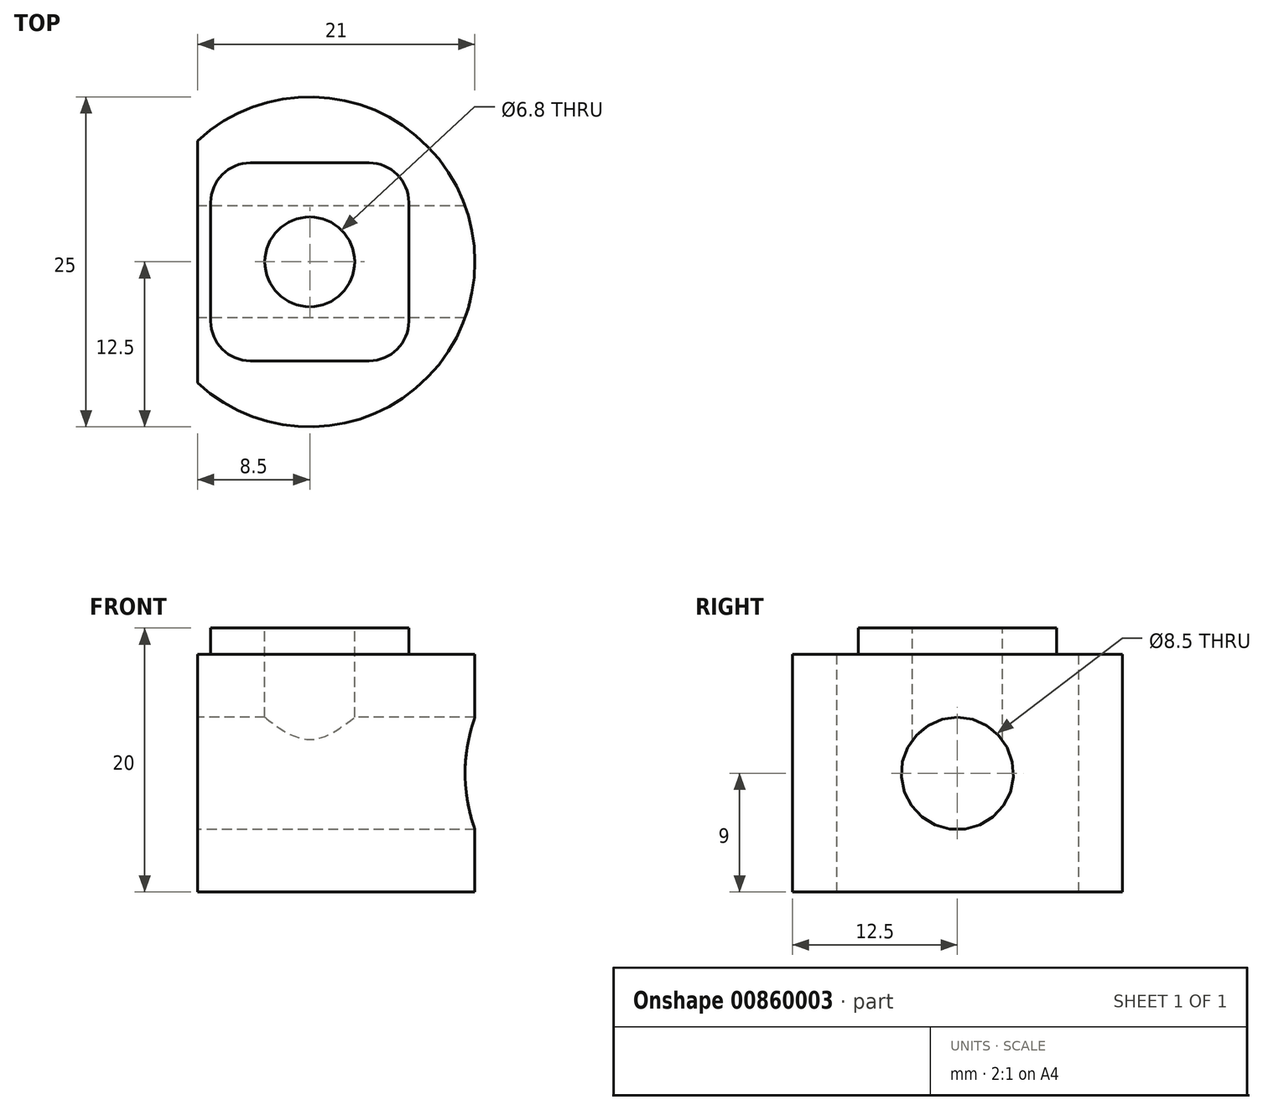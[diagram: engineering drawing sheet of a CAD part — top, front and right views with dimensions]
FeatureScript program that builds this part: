
annotation { "Feature Type Name" : "Feature", "Feature Type Description" : "" }
export const myFeature = defineFeature(function(context is Context, id is Id, definition is map)
    precondition{}
    {
        {
            var Q0;
            Q0=qCreatedBy(makeId("Top.planeOp"),FACE);
            var sketch = newSketch(context, id + "F0", { "sketchPlane" : qUnion([Q0])});
            skArc(sketch, "E0", {"start": v(-8.5, -9.17) * mm, "mid": v(12.5, 0) * mm, "end": v(-8.5, 9.17) * mm});
            skLineSegment(sketch, "E1", {"start": v(-8.5, 9.17) * mm, "end": v(-8.5, -9.17) * mm});
            skSolve(sketch);
        }
        {
            var Q0;
            Q0 = qSketchRegion(id + "F0", true);
            extrude(context, id + "F1", {"entities" : qUnion([Q0]), "depth" : 18 * mm, "offsetDistance" : 25 * mm});
        }
        {
            var Q0;
            Q0=makeQuery(id+"F1.opExtrude","CAP_FACE",FACE,{"disambiguationData":[OSD([sQuery(id+"F0.wireOp",EDGE,"E0"),sQuery(id+"F0.wireOp",EDGE,"E1")])],"isStart":false});
            var sketch = newSketch(context, id + "F2", { "sketchPlane" : qUnion([Q0])});
            skLineSegment(sketch, "E2.bottom", {"start": v(4.5, -7.5) * mm, "end": v(-4.5, -7.5) * mm});
            skLineSegment(sketch, "E2.top", {"start": v(4.5, 7.5) * mm, "end": v(-4.5, 7.5) * mm});
            skLineSegment(sketch, "E2.left", {"start": v(7.5, -4.5) * mm, "end": v(7.5, 4.5) * mm});
            skLineSegment(sketch, "E2.right", {"start": v(-7.5, -4.5) * mm, "end": v(-7.5, 4.5) * mm});
            skPoint(sketch, "E2.middle", {"position": v(0, 0) * mm});
            skPoint(sketch, "E3.visualSharp", {"position": v(-7.5, 7.5) * mm});
            skArc(sketch, "E3.filletArc", {"start": v(-4.5, 7.5) * mm, "mid": v(-6.62, 6.62) * mm, "end": v(-7.5, 4.5) * mm});
            skPoint(sketch, "E4.visualSharp", {"position": v(7.5, 7.5) * mm});
            skArc(sketch, "E4.filletArc", {"start": v(7.5, 4.5) * mm, "mid": v(6.62, 6.62) * mm, "end": v(4.5, 7.5) * mm});
            skPoint(sketch, "E5.visualSharp", {"position": v(7.5, -7.5) * mm});
            skArc(sketch, "E5.filletArc", {"start": v(4.5, -7.5) * mm, "mid": v(6.62, -6.62) * mm, "end": v(7.5, -4.5) * mm});
            skPoint(sketch, "E6.visualSharp", {"position": v(-7.5, -7.5) * mm});
            skArc(sketch, "E6.filletArc", {"start": v(-7.5, -4.5) * mm, "mid": v(-6.62, -6.62) * mm, "end": v(-4.5, -7.5) * mm});
            skSolve(sketch);
        }
        {
            var Q0;
            Q0 = qSketchRegion(id + "F2", true);
            extrude(context, id + "F3", {"entities" : qUnion([Q0]), "operationType" : NewBodyOperationType.ADD, "depth" : 2 * mm, "offsetDistance" : 25 * mm});
        }
        {
            var Q0;
            Q0=makeQuery(id+"F3.opExtrude","CAP_FACE",FACE,{"disambiguationData":[OSD([sQuery(id+"F2.wireOp",EDGE,"E2.bottom"),sQuery(id+"F2.wireOp",EDGE,"E2.top"),sQuery(id+"F2.wireOp",EDGE,"E2.left"),sQuery(id+"F2.wireOp",EDGE,"E2.right"),sQuery(id+"F2.wireOp",EDGE,"E3.filletArc"),sQuery(id+"F2.wireOp",EDGE,"E4.filletArc"),sQuery(id+"F2.wireOp",EDGE,"E5.filletArc"),sQuery(id+"F2.wireOp",EDGE,"E6.filletArc")])],"isStart":false});
            var sketch = newSketch(context, id + "F4", { "sketchPlane" : qUnion([Q0])});
            skPoint(sketch, "E7.0", {"position": v(0, 0) * mm});
            skSolve(sketch);
        }
        {
            var Q0;
            Q0=makeQuery(id+"F1.opExtrude","SWEPT_FACE",FACE,{"disambiguationData":[OSD([sQuery(id+"F0.wireOp",EDGE,"E1")])]});
            var sketch = newSketch(context, id + "F5", { "sketchPlane" : qUnion([Q0])});
            skPoint(sketch, "E8", {"position": v(0, 9) * mm});
            skSolve(sketch);
        }
        {
            var Q0;
            Q0=sQuery(id+"F5.wireOp",VERTEX,"E8");
            var Q1;
            Q1=makeQuery(id+"F1.opExtrude","SWEPT_BODY",BODY,{"disambiguationData":[OSD([sQuery(id+"F0.wireOp",EDGE,"E0"),sQuery(id+"F0.wireOp",EDGE,"E1")])]});
            hole(context, id + "F6", {"style" : HoleStyle.SIMPLE, "endStyle" : HoleEndStyle.THROUGH, "standardTappedOrClearance" : lookupTablePath({ "standard" : "ISO", "engagement" : "75%", "pitch" : "1.5 mm", "size" : "M10", "type" : "Tapped" }), "standardBlindInLast" : lookupTablePath({ "standard" : "ISO", "engagement" : "75%", "pitch" : "1.5 mm", "size" : "M10", "type" : "Tapped" }), "holeDiameter" : 8.5 * mm, "majorDiameter" : 10 * mm, "showTappedDepth" : true, "isTappedThrough" : true, "tappedDepth" : 5.6 * mm, "tapClearance" : 3, "startFromSketch" : true, "locations" : qUnion([Q0]), "scope" : qUnion([Q1])});
        }
        {
            var Q0;
            Q0=sQuery(id+"F4.wireOp",VERTEX,"E7.0");
            var Q1;
            Q1=makeQuery(id+"F1.opExtrude","SWEPT_BODY",BODY,{"disambiguationData":[OSD([sQuery(id+"F0.wireOp",EDGE,"E0"),sQuery(id+"F0.wireOp",EDGE,"E1")])]});
            hole(context, id + "F7", {"style" : HoleStyle.SIMPLE, "endStyle" : HoleEndStyle.BLIND, "standardTappedOrClearance" : lookupTablePath({ "standard" : "ISO", "engagement" : "75%", "pitch" : "1.25 mm", "size" : "M8", "type" : "Tapped" }), "standardBlindInLast" : lookupTablePath({ "standard" : "ISO", "engagement" : "75%", "pitch" : "1.25 mm", "size" : "M8", "type" : "Tapped" }), "holeDiameter" : 6.8 * mm, "majorDiameter" : 8 * mm, "showTappedDepth" : true, "holeDepth" : 10 * mm, "isTappedThrough" : true, "tappedDepth" : 10 * mm, "tapClearance" : 0, "startFromSketch" : true, "locations" : qUnion([Q0]), "scope" : qUnion([Q1])});
        }
    });
